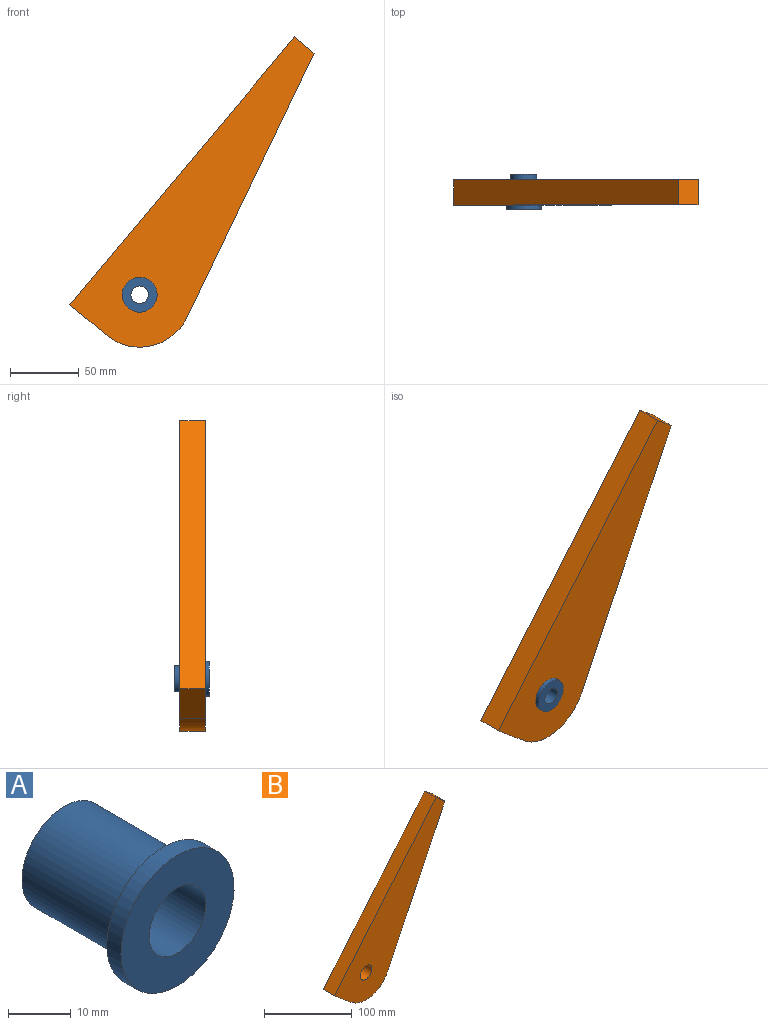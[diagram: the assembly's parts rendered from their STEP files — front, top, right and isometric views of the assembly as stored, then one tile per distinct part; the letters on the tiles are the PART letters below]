
ASSEMBLY  parts=2 mates=1
PART A: 6 faces, bbox 25.4x25.4x25.4 mm
  f0: plane 19.05x19.05mm, normal (0,1,0), area 158.3mm2, adj f2,f4
  f1: cylinder r=12.7mm len=25.4mm, axis (0,1,0), area 253.4mm2, adj f3,f5
  f2: cylinder r=6.35mm len=25.4mm, axis (0,1,0), area 1013.4mm2, adj f0,f3
  f3: plane 25.4x25.4mm, normal (0,-1,0), area 380mm2, adj f1,f2
  f4: cylinder r=9.53mm len=22.23mm, axis (0,1,0), area 1330.1mm2, adj f0,f5
  f5: plane 25.4x25.4mm, normal (0,1,0), area 221.7mm2, adj f1,f4
PART B: 8 faces, bbox 177.3x18.3x225.4 mm
  f0: cylinder r=9.53mm len=19.05mm, axis (0,1,0), area 1094.5mm2, adj f1,f2
  f1: plane 225.45x177.28mm, normal (0,-1,0), area 12060.1mm2, adj f0,f3,f4,f5,f6,f7
  f2: plane 225.45x177.28mm, normal (0,1,0), area 12060.1mm2, adj f0,f3,f4,f5,f6,f7
  f3: plane 192.09x92.27mm, normal (0.9,0,-0.43), area 3897.2mm2, adj f1,f2,f4,f7
  f4: plane 18.29x14.01mm, normal (0.64,0,0.77), area 334.5mm2, adj f1,f2,f3,f5
  f5: plane 194.58x163.27mm, normal (-0.77,0,0.64), area 4645.2mm2, adj f1,f2,f4,f6
  f6: plane 26.17x21.96mm, normal (-0.64,0,-0.77), area 624.8mm2, adj f1,f2,f5,f7
  f7: cylinder r=38.1mm len=58.83mm, axis (0,1,0), area 1268.9mm2, adj f1,f2,f3,f6
PLACE A at identity
PLACE B t=(0,468.25,0)mm
MATE fastened B.f0 <-> A.f1  axis (0,1,0) through (-346.74,-22.22,396.31)mm
